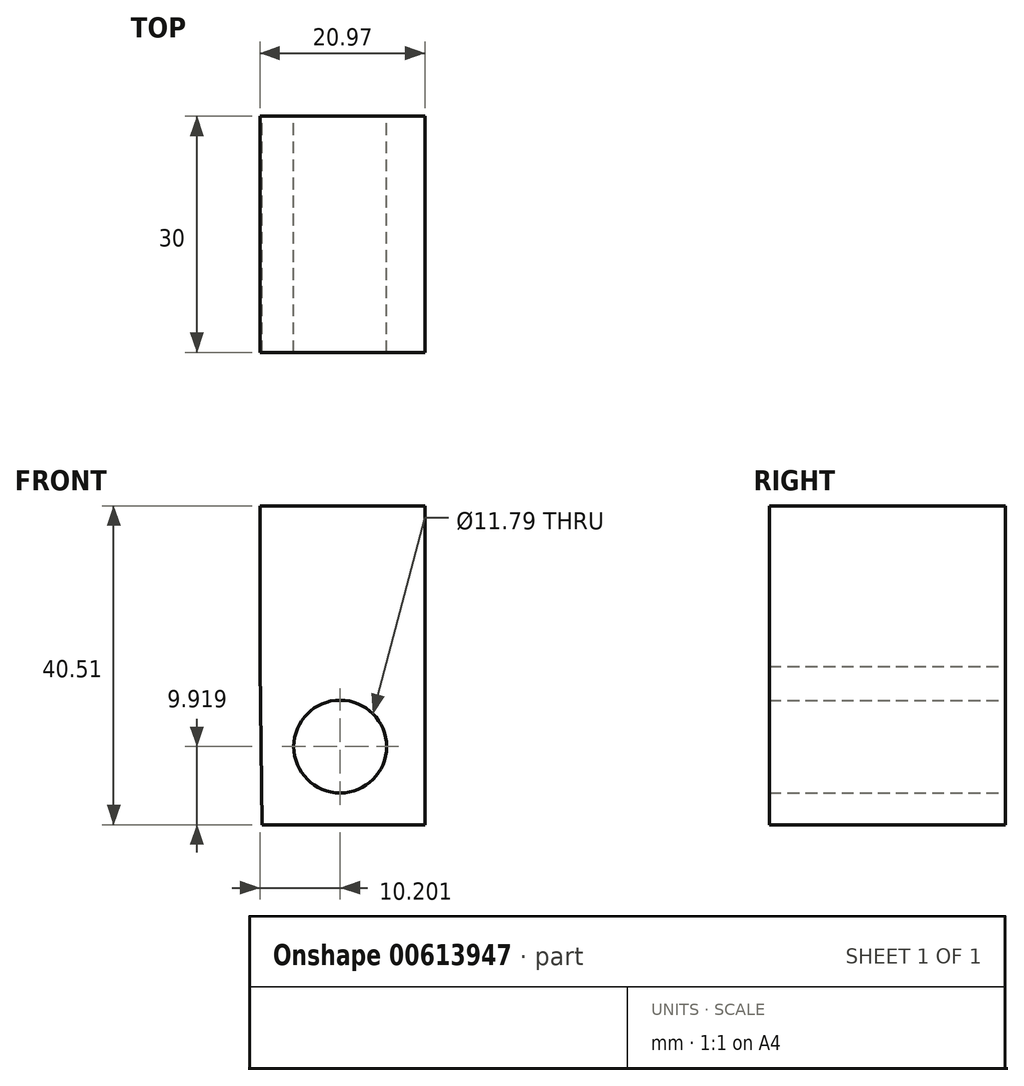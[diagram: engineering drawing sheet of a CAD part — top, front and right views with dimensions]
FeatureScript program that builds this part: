
annotation { "Feature Type Name" : "Feature", "Feature Type Description" : "" }
export const myFeature = defineFeature(function(context is Context, id is Id, definition is map)
    precondition{}
    {
        {
            var Q0;
            Q0=qCreatedBy(makeId("Front.planeOp"),FACE);
            var sketch = newSketch(context, id + "F0", { "sketchPlane" : qUnion([Q0])});
            skLineSegment(sketch, "E0", {"start": v(-36.68, -46.32) * mm, "end": v(-16, -46.32) * mm});
            skLineSegment(sketch, "E1", {"start": v(-16, -46.32) * mm, "end": v(-16, -26.2) * mm});
            skLineSegment(sketch, "E2", {"start": v(-16, -26.2) * mm, "end": v(-36.97, -26.2) * mm});
            skLineSegment(sketch, "E3", {"start": v(-36.97, -26.2) * mm, "end": v(-36.68, -46.32) * mm});
            skLineSegment(sketch, "E4", {"start": v(-36.97, -26.2) * mm, "end": v(-36.97, -5.8) * mm});
            skLineSegment(sketch, "E5", {"start": v(-36.97, -5.8) * mm, "end": v(-16, -5.8) * mm});
            skLineSegment(sketch, "E6", {"start": v(-16, -5.8) * mm, "end": v(-16, -26.2) * mm});
            skCircle(sketch, "E7", {"center": v(-26.77, -36.4) * mm, "radius": 5.9 * mm});
            skSolve(sketch);
        }
        {
            var Q0;
            Q0 = qSketchRegion(id + "F0", true);
            extrude(context, id + "F1", {"entities" : qUnion([Q0]), "depth" : 30 * mm, "offsetDistance" : 25 * mm});
        }
    });
